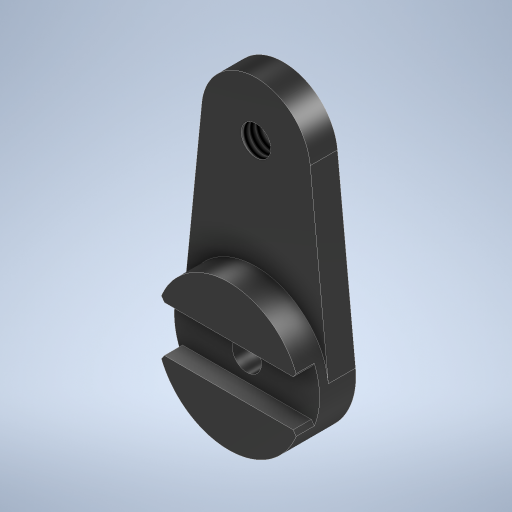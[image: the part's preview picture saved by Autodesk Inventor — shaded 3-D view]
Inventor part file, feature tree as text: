
AUTODESK INVENTOR PART (.ipt)
format: ipt  version: 2024.2 (Build 282272000, 272)  size: 292,864 bytes
history: native  units: mm
features: other x3, chamfer x1, plane x1
ambient origin geometry x8: Origin, YZ Plane, XZ Plane, XY Plane, X Axis, Y Axis, Z Axis, Center Point
bodies: Solid1 (feature_tree)
feature tree (5):
  other  "LongCrankFrameBasis.ipt"
  chamfer  "C0.5"  Distance=10.0mm
  plane  "Work Plane1"
  other  "Solid1::LongCrankFrameBasis.ipt"
  other  "TaggingFeature1"
